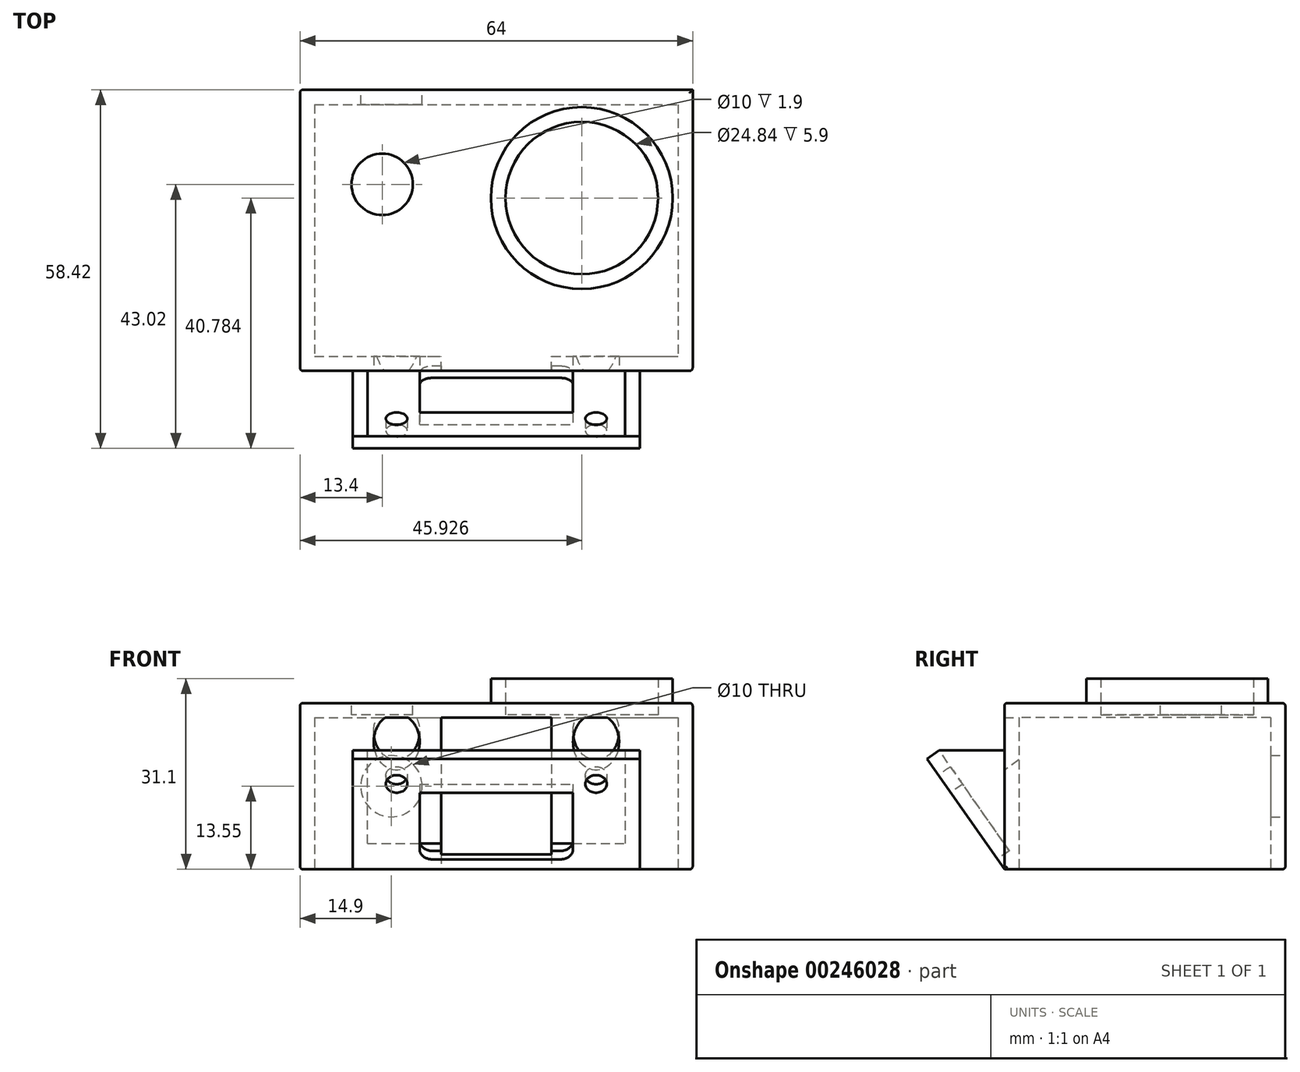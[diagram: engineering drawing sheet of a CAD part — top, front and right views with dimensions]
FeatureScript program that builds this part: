
annotation { "Feature Type Name" : "Feature", "Feature Type Description" : "" }
export const myFeature = defineFeature(function(context is Context, id is Id, definition is map)
    precondition{}
    {
        {
            assignVariable(context, id + "F0", {"name" : "goproThickness", "anyValue" : 24.7});
        }
        {
            assignVariable(context, id + "F1", {"name" : "lensDepth", "anyValue" : 4});
        }
        {
            assignVariable(context, id + "F2", {"name" : "caseThickness", "anyValue" : 2.4});
        }
        {
            assignVariable(context, id + "F3", {"name" : "webThickness", "anyValue" : 0.5});
        }
        {
            assignVariable(context, id + "F4", {"name" : "cameraTilt", "anyValue" : 35});
        }
        {
            var Q0;
            Q0=qCreatedBy(makeId("Top.planeOp"),FACE);
            var sketch = newSketch(context, id + "F5", { "sketchPlane" : qUnion([Q0])});
            skLineSegment(sketch, "E0.bottom", {"start": v(-29.6, 20.5) * mm, "end": v(29.6, 20.5) * mm});
            skLineSegment(sketch, "E0.top", {"start": v(-29.6, -20.5) * mm, "end": v(29.6, -20.5) * mm});
            skLineSegment(sketch, "E0.left", {"start": v(-29.6, 20.5) * mm, "end": v(-29.6, -20.5) * mm});
            skLineSegment(sketch, "E0.right", {"start": v(29.6, 20.5) * mm, "end": v(29.6, -20.5) * mm});
            skPoint(sketch, "E0.middle", {"position": v(0, 0) * mm});
            skLineSegment(sketch, "E1.0", {"start": v(-32, 22.9) * mm, "end": v(32, 22.9) * mm});
            skLineSegment(sketch, "E1.1", {"start": v(-32, 22.9) * mm, "end": v(-32, -22.9) * mm});
            skLineSegment(sketch, "E1.2", {"start": v(-32, -22.9) * mm, "end": v(32, -22.9) * mm});
            skLineSegment(sketch, "E1.3", {"start": v(32, 22.9) * mm, "end": v(32, -22.9) * mm});
            skSolve(sketch);
        }
        {
            var Q0;
            Q0 = qSketchRegion(id + "F5", true);
            extrude(context, id + "F6", {"entities" : qUnion([Q0]), "depth" : (getVariable(context, 'goproThickness')) * mm});
        }
        {
            var Q0;
            Q0=makeQuery(id+"F6.opExtrude","CAP_FACE",FACE,{"disambiguationData":[OSD([sQuery(id+"F5.wireOp",EDGE,"E0.bottom"),sQuery(id+"F5.wireOp",EDGE,"E0.top"),sQuery(id+"F5.wireOp",EDGE,"E0.left"),sQuery(id+"F5.wireOp",EDGE,"E0.right"),sQuery(id+"F5.wireOp",EDGE,"E1.0"),sQuery(id+"F5.wireOp",EDGE,"E1.1"),sQuery(id+"F5.wireOp",EDGE,"E1.2"),sQuery(id+"F5.wireOp",EDGE,"E1.3")])],"isStart":false});
            var sketch = newSketch(context, id + "F7", { "sketchPlane" : qUnion([Q0])});
            skLineSegment(sketch, "E2.bottom", {"start": v(-29.6, 20.5) * mm, "end": v(29.6, 20.5) * mm});
            skLineSegment(sketch, "E2.top", {"start": v(-29.6, -20.5) * mm, "end": v(29.6, -20.5) * mm});
            skLineSegment(sketch, "E2.left", {"start": v(-29.6, 20.5) * mm, "end": v(-29.6, -20.5) * mm});
            skLineSegment(sketch, "E2.right", {"start": v(29.6, 20.5) * mm, "end": v(29.6, -20.5) * mm});
            skPoint(sketch, "E2.middle", {"position": v(0, 0) * mm});
            skLineSegment(sketch, "E3.bottom", {"start": v(-32, 22.9) * mm, "end": v(32, 22.9) * mm});
            skLineSegment(sketch, "E3.top", {"start": v(-32, -22.9) * mm, "end": v(32, -22.9) * mm});
            skLineSegment(sketch, "E3.left", {"start": v(-32, 22.9) * mm, "end": v(-32, -22.9) * mm});
            skLineSegment(sketch, "E3.right", {"start": v(32, 22.9) * mm, "end": v(32, -22.9) * mm});
            skSolve(sketch);
        }
        {
            var Q0;
            Q0 = qSketchRegion(id + "F7", true);
            var Q1;
            Q1=makeQuery(id+"F7.imprint","IMPRINT",FACE,{"disambiguationData":[TD([[makeQuery(id+"F7.imprint","IMPRINT",EDGE,{"derivedFrom":sQuery(id+"F7.wireOp",EDGE,"E2.bottom")}),-1.0]])]});
            extrude(context, id + "F8", {"entities" : qUnion([Q0, Q1]), "operationType" : NewBodyOperationType.ADD, "depth" : (getVariable(context, 'caseThickness')) * mm});
        }
        {
            var Q0;
            Q0=makeQuery(id+"F8.opExtrude","CAP_FACE",FACE,{"disambiguationData":[OSD([sQuery(id+"F7.wireOp",EDGE,"E3.bottom"),sQuery(id+"F7.wireOp",EDGE,"E3.top"),sQuery(id+"F7.wireOp",EDGE,"E3.left"),sQuery(id+"F7.wireOp",EDGE,"E3.right")])],"isStart":false});
            var sketch = newSketch(context, id + "F9", { "sketchPlane" : qUnion([Q0])});
            skCircle(sketch, "E4", {"center": v(-18.6, 7.5) * mm, "radius": 5 * mm});
            skSolve(sketch);
        }
        {
            var Q0;
            Q0 = qSketchRegion(id + "F9", true);
            extrude(context, id + "F10", {"entities" : qUnion([Q0]), "operationType" : NewBodyOperationType.REMOVE, "oppositeDirection" : true, "depth" : (getVariable(context, 'caseThickness') - getVariable(context, 'webThickness')) * mm});
        }
        {
            var Q0;
            Q0=makeQuery(id+"F8.opExtrude","CAP_FACE",FACE,{"disambiguationData":[OSD([sQuery(id+"F7.wireOp",EDGE,"E3.bottom"),sQuery(id+"F7.wireOp",EDGE,"E3.top"),sQuery(id+"F7.wireOp",EDGE,"E3.left"),sQuery(id+"F7.wireOp",EDGE,"E3.right")])],"isStart":false});
            var sketch = newSketch(context, id + "F11", { "sketchPlane" : qUnion([Q0])});
            skCircle(sketch, "E5", {"center": v(13.93, 5.26) * mm, "radius": 12.42 * mm});
            skCircle(sketch, "E6", {"center": v(13.93, 5.26) * mm, "radius": 14.82 * mm});
            skSolve(sketch);
        }
        {
            var Q0;
            Q0 = qSketchRegion(id + "F11", true);
            extrude(context, id + "F12", {"entities" : qUnion([Q0]), "operationType" : NewBodyOperationType.ADD, "depth" : (getVariable(context, 'lensDepth')) * mm});
        }
        {
            var Q0;
            Q0=makeQuery(id+"F12.boolean.opBoolean","SPLIT",FACE,{"disambiguationData":[TD([makeQuery(id+"F12.opExtrude","SWEPT_FACE",FACE,{"disambiguationData":[OSD([sQuery(id+"F11.wireOp",EDGE,"E5")])]})])],"derivedFrom":makeQuery(id+"F8.opExtrude","CAP_FACE",FACE,{"disambiguationData":[OSD([sQuery(id+"F7.wireOp",EDGE,"E3.bottom"),sQuery(id+"F7.wireOp",EDGE,"E3.top"),sQuery(id+"F7.wireOp",EDGE,"E3.left"),sQuery(id+"F7.wireOp",EDGE,"E3.right")])],"isStart":false})});
            extrude(context, id + "F13", {"entities" : qUnion([Q0]), "operationType" : NewBodyOperationType.REMOVE, "oppositeDirection" : true, "depth" : (getVariable(context, 'caseThickness') - getVariable(context, 'webThickness')) * mm});
        }
        {
            var Q0;
            Q0=makeQuery(id+"F8.boolean.opBoolean","MERGE",FACE,{"derivedFrom":[makeQuery(id+"F6.opExtrude","SWEPT_FACE",FACE,{"disambiguationData":[OSD([sQuery(id+"F5.wireOp",EDGE,"E1.0")])]}),makeQuery(id+"F8.opExtrude","SWEPT_FACE",FACE,{"disambiguationData":[OSD([sQuery(id+"F7.wireOp",EDGE,"E3.bottom")])]})]});
            var sketch = newSketch(context, id + "F14", { "sketchPlane" : qUnion([Q0])});
            skCircle(sketch, "E7", {"center": v(17.1, 13.55) * mm, "radius": 5 * mm});
            skPoint(sketch, "E7.centerSnap0", {"position": v(32, 13.55) * mm});
            skSolve(sketch);
        }
        {
            var Q0;
            Q0 = qSketchRegion(id + "F14", true);
            extrude(context, id + "F15", {"entities" : qUnion([Q0]), "operationType" : NewBodyOperationType.REMOVE, "oppositeDirection" : true, "depth" : (getVariable(context, 'caseThickness')) * mm});
        }
        {
            var Q0;
            Q0=makeQuery(id+"F6.opExtrude","CAP_EDGE",EDGE,{"disambiguationData":[OSD([sQuery(id+"F5.wireOp",EDGE,"E1.2")])],"isStart":true});
            cPlane(context, id + "F16", {"entities" : qUnion([Q0]), "cplaneType" : CPlaneType.LINE_ANGLE, "offset" : 25 * mm, "angle" : (getVariable(context, 'cameraTilt')) * degree, "width" : 150 * mm, "height" : 150 * mm});
        }
        {
            var Q0;
            Q0=qCreatedBy(id+"F16.planeOp",FACE);
            var sketch = newSketch(context, id + "F17", { "sketchPlane" : qUnion([Q0])});
            skLineSegment(sketch, "E8", {"start": v(0, 13.13) * mm, "end": v(21, 13.13) * mm});
            skLineSegment(sketch, "E9", {"start": v(21, 13.13) * mm, "end": v(21, 35.13) * mm});
            skLineSegment(sketch, "E10", {"start": v(21, 35.13) * mm, "end": v(-21, 35.13) * mm});
            skLineSegment(sketch, "E11", {"start": v(-21, 35.13) * mm, "end": v(-21, 13.13) * mm});
            skLineSegment(sketch, "E12", {"start": v(-21, 13.13) * mm, "end": v(0, 13.13) * mm});
            skLineSegment(sketch, "E13", {"start": v(0, 35.13) * mm, "end": v(0, 24.13) * mm});
            skPoint(sketch, "E13.endSnap0", {"position": v(21, 24.13) * mm});
            skLineSegment(sketch, "E14", {"start": v(0, 24.13) * mm, "end": v(0, 13.13) * mm});
            skCircle(sketch, "E15", {"center": v(16.25, 30.13) * mm, "radius": 1.75 * mm});
            skCircle(sketch, "E16.MirrorC", {"center": v(-16.25, 30.13) * mm, "radius": 1.75 * mm});
            skSolve(sketch);
        }
        {
            var Q0;
            Q0=makeQuery(id+"F17.imprint","IMPRINT",FACE,{"disambiguationData":[TD([[makeQuery(id+"F17.imprint","IMPRINT",EDGE,{"derivedFrom":sQuery(id+"F17.wireOp",EDGE,"E8")}),1.0]])]});
            var Q1;
            {var subQ0=sQuery(id+"F17.wireOp",EDGE,"E11");Q1=makeQuery(id+"F17.imprint","IMPRINT",FACE,{"disambiguationData":[TD([[makeQuery(id+"F17.imprint","IMPRINT",EDGE,{"derivedFrom":subQ0}),1.0]])]});}
            extrude(context, id + "F18", {"entities" : qUnion([Q0, Q1]), "operationType" : NewBodyOperationType.ADD, "depth" : (getVariable(context, 'caseThickness')) * mm});
        }
        {
            var Q0;
            Q0=makeQuery(id+"F18.opExtrude","SWEPT_FACE",FACE,{"disambiguationData":[OSD([sQuery(id+"F17.wireOp",EDGE,"E9")])]});
            var sketch = newSketch(context, id + "F19", { "sketchPlane" : qUnion([Q0])});
            skLineSegment(sketch, "E17", {"start": v(35.52, 18.02) * mm, "end": v(33.55, 19.4) * mm});
            skLineSegment(sketch, "E18", {"start": v(22.9, 0) * mm, "end": v(35.52, 18.02) * mm});
            skLineSegment(sketch, "E19", {"start": v(33.55, 19.4) * mm, "end": v(22.9, 19.4) * mm});
            skLineSegment(sketch, "E20", {"start": v(22.9, 19.4) * mm, "end": v(22.9, 0) * mm});
            skSolve(sketch);
        }
        {
            var Q0;
            Q0 = qSketchRegion(id + "F19", true);
            extrude(context, id + "F20", {"entities" : qUnion([Q0]), "operationType" : NewBodyOperationType.ADD, "depth" : (getVariable(context, 'caseThickness')) * mm});
        }
        {
            var Q0;
            Q0=makeQuery(id+"F18.opExtrude","SWEPT_FACE",FACE,{"disambiguationData":[OSD([sQuery(id+"F17.wireOp",EDGE,"E11")])]});
            var sketch = newSketch(context, id + "F21", { "sketchPlane" : qUnion([Q0])});
            skLineSegment(sketch, "E21", {"start": v(-22.9, 0) * mm, "end": v(-35.52, 18.02) * mm});
            skLineSegment(sketch, "E22", {"start": v(-35.52, 18.02) * mm, "end": v(-33.55, 19.4) * mm});
            skLineSegment(sketch, "E23", {"start": v(-33.55, 19.4) * mm, "end": v(-22.9, 19.4) * mm});
            skLineSegment(sketch, "E24", {"start": v(-22.9, 19.4) * mm, "end": v(-22.9, 0) * mm});
            skSolve(sketch);
        }
        {
            var Q0;
            Q0 = qSketchRegion(id + "F21", true);
            extrude(context, id + "F22", {"entities" : qUnion([Q0]), "operationType" : NewBodyOperationType.ADD, "depth" : (getVariable(context, 'caseThickness')) * mm});
        }
        {
            var Q0;
            Q0=makeQuery(id+"F22.boolean.opBoolean","MERGE",FACE,{"derivedFrom":[makeQuery(id+"F20.boolean.opBoolean","MERGE",FACE,{"derivedFrom":[makeQuery(id+"F18.opExtrude","CAP_FACE",FACE,{"disambiguationData":[OSD([sQuery(id+"F17.wireOp",EDGE,"E8"),sQuery(id+"F17.wireOp",EDGE,"E9"),sQuery(id+"F17.wireOp",EDGE,"E10"),sQuery(id+"F17.wireOp",EDGE,"E11"),sQuery(id+"F17.wireOp",EDGE,"E12"),sQuery(id+"F17.wireOp",EDGE,"E15"),sQuery(id+"F17.wireOp",EDGE,"E16.MirrorC")])],"isStart":true}),makeQuery(id+"F20.opExtrude","SWEPT_FACE",FACE,{"disambiguationData":[OSD([sQuery(id+"F19.wireOp",EDGE,"E18")])]})]}),makeQuery(id+"F22.opExtrude","SWEPT_FACE",FACE,{"disambiguationData":[OSD([sQuery(id+"F21.wireOp",EDGE,"E21")])]})]});
            var sketch = newSketch(context, id + "F23", { "sketchPlane" : qUnion([Q0])});
            skCircle(sketch, "E25", {"center": v(-16.25, 30.13) * mm, "radius": 1.75 * mm});
            skCircle(sketch, "E26.MirrorC", {"center": v(16.25, 30.13) * mm, "radius": 1.75 * mm});
            skSolve(sketch);
        }
        {
            var Q0;
            Q0 = qSketchRegion(id + "F23", true);
            var Q1;
            Q1=makeQuery(id+"F8.opExtrude","CAP_FACE",FACE,{"disambiguationData":[OSD([sQuery(id+"F7.wireOp",EDGE,"E3.bottom"),sQuery(id+"F7.wireOp",EDGE,"E3.top"),sQuery(id+"F7.wireOp",EDGE,"E3.left"),sQuery(id+"F7.wireOp",EDGE,"E3.right")])],"isStart":true});
            extrude(context, id + "F24", {"entities" : qUnion([Q0]), "operationType" : NewBodyOperationType.REMOVE, "endBound" : BoundingType.UP_TO_SURFACE, "oppositeDirection" : true, "endBoundEntityFace" : qUnion([Q1]), "depth" : 25 * mm});
        }
        {
            var Q0;
            Q0=makeQuery(id+"F8.opExtrude","CAP_EDGE",EDGE,{"disambiguationData":[OSD([sQuery(id+"F7.wireOp",EDGE,"E3.left")])],"isStart":false});
            var Q1;
            Q1=makeQuery(id+"F8.opExtrude","CAP_EDGE",EDGE,{"disambiguationData":[OSD([sQuery(id+"F7.wireOp",EDGE,"E3.top")])],"isStart":false});
            var Q2;
            Q2=makeQuery(id+"F8.opExtrude","CAP_EDGE",EDGE,{"disambiguationData":[OSD([sQuery(id+"F7.wireOp",EDGE,"E3.right")])],"isStart":false});
            var Q3;
            Q3=makeQuery(id+"F8.opExtrude","CAP_EDGE",EDGE,{"disambiguationData":[OSD([sQuery(id+"F7.wireOp",EDGE,"E3.bottom")])],"isStart":false});
            var Q4;
            Q4=makeQuery(id+"F10.boolean.opBoolean","COPY",EDGE,{"derivedFrom":makeQuery(id+"F10.opExtrude","CAP_EDGE",EDGE,{"disambiguationData":[OSD([sQuery(id+"F9.wireOp",EDGE,"E4")])],"isStart":true})});
            var Q5;
            Q5=makeQuery(id+"F6.opExtrude","CAP_EDGE",EDGE,{"disambiguationData":[OSD([sQuery(id+"F5.wireOp",EDGE,"E1.3")])],"isStart":true});
            var Q6;
            Q6=makeQuery(id+"F6.opExtrude","CAP_EDGE",EDGE,{"disambiguationData":[OSD([sQuery(id+"F5.wireOp",EDGE,"E1.0")])],"isStart":true});
            var Q7;
            Q7=makeQuery(id+"F8.boolean.opBoolean","MERGE",EDGE,{"derivedFrom":[makeQuery(id+"F6.opExtrude","SWEPT_EDGE",EDGE,{"disambiguationData":[OSD([sQuery(id+"F5.wireOp",EDGE,"E1.0"),sQuery(id+"F5.wireOp",EDGE,"E1.1")])]}),makeQuery(id+"F8.opExtrude","SWEPT_EDGE",EDGE,{"disambiguationData":[OSD([sQuery(id+"F7.wireOp",EDGE,"E3.bottom"),sQuery(id+"F7.wireOp",EDGE,"E3.left")])]})]});
            var Q8;
            Q8=makeQuery(id+"F6.opExtrude","CAP_EDGE",EDGE,{"disambiguationData":[OSD([sQuery(id+"F5.wireOp",EDGE,"E1.1")])],"isStart":true});
            var Q9;
            Q9=makeQuery(id+"F8.boolean.opBoolean","MERGE",EDGE,{"derivedFrom":[makeQuery(id+"F6.opExtrude","SWEPT_EDGE",EDGE,{"disambiguationData":[OSD([sQuery(id+"F5.wireOp",EDGE,"E1.1"),sQuery(id+"F5.wireOp",EDGE,"E1.2")])]}),makeQuery(id+"F8.opExtrude","SWEPT_EDGE",EDGE,{"disambiguationData":[OSD([sQuery(id+"F7.wireOp",EDGE,"E3.top"),sQuery(id+"F7.wireOp",EDGE,"E3.left")])]})]});
            var Q10;
            Q10=makeQuery(id+"F8.boolean.opBoolean","MERGE",EDGE,{"derivedFrom":[makeQuery(id+"F6.opExtrude","SWEPT_EDGE",EDGE,{"disambiguationData":[OSD([sQuery(id+"F5.wireOp",EDGE,"E1.2"),sQuery(id+"F5.wireOp",EDGE,"E1.3")])]}),makeQuery(id+"F8.opExtrude","SWEPT_EDGE",EDGE,{"disambiguationData":[OSD([sQuery(id+"F7.wireOp",EDGE,"E3.top"),sQuery(id+"F7.wireOp",EDGE,"E3.right")])]})]});
            fillet(context, id + "F25", {"entities" : qUnion([Q0, Q1, Q2, Q3, Q4, Q5, Q6, Q7, Q8, Q9, Q10]), "radius" : 0.5 * mm, "tangentPropagation" : true, "allowEdgeOverflow" : false});
        }
        {
            var Q0;
            Q0=makeQuery(id+"F6.opExtrude","CAP_FACE",FACE,{"disambiguationData":[OSD([sQuery(id+"F5.wireOp",EDGE,"E0.bottom"),sQuery(id+"F5.wireOp",EDGE,"E0.top"),sQuery(id+"F5.wireOp",EDGE,"E0.left"),sQuery(id+"F5.wireOp",EDGE,"E0.right"),sQuery(id+"F5.wireOp",EDGE,"E1.0"),sQuery(id+"F5.wireOp",EDGE,"E1.1"),sQuery(id+"F5.wireOp",EDGE,"E1.2"),sQuery(id+"F5.wireOp",EDGE,"E1.3")])],"isStart":true});
            var sketch = newSketch(context, id + "F26", { "sketchPlane" : qUnion([Q0])});
            skLineSegment(sketch, "E27.bottom", {"start": v(-9, 22.9) * mm, "end": v(9, 22.9) * mm});
            skLineSegment(sketch, "E27.top", {"start": v(-9, 20.5) * mm, "end": v(9, 20.5) * mm});
            skLineSegment(sketch, "E27.left", {"start": v(-9, 22.9) * mm, "end": v(-9, 20.5) * mm});
            skLineSegment(sketch, "E27.right", {"start": v(9, 22.9) * mm, "end": v(9, 20.5) * mm});
            skPoint(sketch, "E27.middle", {"position": v(0, 21.7) * mm});
            skSolve(sketch);
        }
        {
            var Q0;
            Q0 = qSketchRegion(id + "F26", true);
            var Q1;
            Q1=makeQuery(id+"F8.opExtrude","CAP_FACE",FACE,{"disambiguationData":[OSD([sQuery(id+"F7.wireOp",EDGE,"E3.bottom"),sQuery(id+"F7.wireOp",EDGE,"E3.top"),sQuery(id+"F7.wireOp",EDGE,"E3.left"),sQuery(id+"F7.wireOp",EDGE,"E3.right")])],"isStart":true});
            extrude(context, id + "F27", {"entities" : qUnion([Q0]), "operationType" : NewBodyOperationType.REMOVE, "endBound" : BoundingType.UP_TO_SURFACE, "oppositeDirection" : true, "endBoundEntityFace" : qUnion([Q1]), "depth" : 25 * mm});
        }
        {
            var Q0;
            Q0=makeQuery(id+"F18.opExtrude","CAP_FACE",FACE,{"disambiguationData":[OSD([sQuery(id+"F17.wireOp",EDGE,"E8"),sQuery(id+"F17.wireOp",EDGE,"E9"),sQuery(id+"F17.wireOp",EDGE,"E10"),sQuery(id+"F17.wireOp",EDGE,"E11"),sQuery(id+"F17.wireOp",EDGE,"E12"),sQuery(id+"F17.wireOp",EDGE,"E15"),sQuery(id+"F17.wireOp",EDGE,"E16.MirrorC")])],"isStart":false});
            var sketch = newSketch(context, id + "F28", { "sketchPlane" : qUnion([Q0])});
            skCircle(sketch, "E28", {"center": v(16.25, 30.13) * mm, "radius": 3.75 * mm});
            skCircle(sketch, "E29.MirrorC", {"center": v(-16.25, 30.13) * mm, "radius": 3.75 * mm});
            skSolve(sketch);
        }
        {
            var Q0;
            Q0 = qSketchRegion(id + "F28", true);
            var Q1;
            {var subQ0=sQuery(id+"F7.wireOp",EDGE,"E3.right");var subQ1=sQuery(id+"F7.wireOp",EDGE,"E3.left");var subQ2=sQuery(id+"F7.wireOp",EDGE,"E3.top");var subQ3=sQuery(id+"F7.wireOp",EDGE,"E3.bottom");Q1=makeQuery(id+"F27.boolean.opBoolean","MERGE",FACE,{"derivedFrom":[makeQuery(id+"F8.opExtrude","CAP_FACE",FACE,{"disambiguationData":[OSD([subQ3,subQ2,subQ1,subQ0])],"isStart":true}),makeQuery(id+"F27.opExtrude","CAP_FACE",FACE,{"disambiguationData":[OSD([subQ3,subQ2,subQ1,subQ0])],"isStart":false})]});}
            extrude(context, id + "F29", {"entities" : qUnion([Q0]), "operationType" : NewBodyOperationType.REMOVE, "endBound" : BoundingType.UP_TO_SURFACE, "endBoundEntityFace" : qUnion([Q1]), "depth" : 25 * mm});
        }
        {
            var Q0;
            Q0=makeQuery(id+"F22.boolean.opBoolean","MERGE",FACE,{"derivedFrom":[makeQuery(id+"F20.boolean.opBoolean","MERGE",FACE,{"derivedFrom":[makeQuery(id+"F18.opExtrude","CAP_FACE",FACE,{"disambiguationData":[OSD([sQuery(id+"F17.wireOp",EDGE,"E8"),sQuery(id+"F17.wireOp",EDGE,"E9"),sQuery(id+"F17.wireOp",EDGE,"E10"),sQuery(id+"F17.wireOp",EDGE,"E11"),sQuery(id+"F17.wireOp",EDGE,"E12"),sQuery(id+"F17.wireOp",EDGE,"E15"),sQuery(id+"F17.wireOp",EDGE,"E16.MirrorC")])],"isStart":true}),makeQuery(id+"F20.opExtrude","SWEPT_FACE",FACE,{"disambiguationData":[OSD([sQuery(id+"F19.wireOp",EDGE,"E18")])]})]}),makeQuery(id+"F22.opExtrude","SWEPT_FACE",FACE,{"disambiguationData":[OSD([sQuery(id+"F21.wireOp",EDGE,"E21")])]})]});
            var sketch = newSketch(context, id + "F30", { "sketchPlane" : qUnion([Q0])});
            skPoint(sketch, "E30", {"position": v(-16.25, 30.13) * mm});
            skPoint(sketch, "E31", {"position": v(16.25, 30.13) * mm});
            skLineSegment(sketch, "E32", {"start": v(-12.5, 28.38) * mm, "end": v(-12.5, 15.13) * mm});
            skLineSegment(sketch, "E33", {"start": v(-12.5, 15.13) * mm, "end": v(0, 15.13) * mm});
            skLineSegment(sketch, "E34", {"start": v(0, 15.13) * mm, "end": v(12.5, 15.13) * mm});
            skLineSegment(sketch, "E35", {"start": v(12.5, 15.13) * mm, "end": v(12.5, 28.38) * mm});
            skLineSegment(sketch, "E36", {"start": v(-12.5, 28.38) * mm, "end": v(12.5, 28.38) * mm});
            skLineSegment(sketch, "E37", {"start": v(-12.5, 28.38) * mm, "end": v(-20.09, 28.38) * mm});
            skSolve(sketch);
        }
        {
            var Q0;
            Q0 = qSketchRegion(id + "F30", true);
            var Q1;
            {var subQ1=sQuery(id+"F30.wireOp",EDGE,"BaOD2BEO-CHPW-Bun6-DBrZ-VnkcG4sa4ueP");Q1=makeQuery(id+"F30.imprint","IMPRINT",FACE,{"disambiguationData":[TD([[makeQuery(id+"F30.imprint","IMPRINT",EDGE,{"derivedFrom":subQ1}),1.0]])]});}
            extrude(context, id + "F31", {"entities" : qUnion([Q0, Q1]), "operationType" : NewBodyOperationType.REMOVE, "oppositeDirection" : true, "depth" : (getVariable(context, 'caseThickness')) * mm});
        }
        {
            var Q0;
            Q0=makeQuery(id+"F31.boolean.opBoolean","COPY",EDGE,{"derivedFrom":makeQuery(id+"F31.opExtrude","SWEPT_EDGE",EDGE,{"disambiguationData":[OSD([sQuery(id+"F30.wireOp",EDGE,"E32"),sQuery(id+"F30.wireOp",EDGE,"E33")])]})});
            var Q1;
            Q1=makeQuery(id+"F31.boolean.opBoolean","COPY",EDGE,{"derivedFrom":makeQuery(id+"F31.opExtrude","SWEPT_EDGE",EDGE,{"disambiguationData":[OSD([sQuery(id+"F30.wireOp",EDGE,"E34"),sQuery(id+"F30.wireOp",EDGE,"E35")])]})});
            fillet(context, id + "F32", {"entities" : qUnion([Q0, Q1]), "radius" : 2 * mm, "tangentPropagation" : true, "allowEdgeOverflow" : false});
        }
        {
            var Q0;
            Q0=makeQuery(id+"F12.opExtrude","CAP_FACE",FACE,{"disambiguationData":[OSD([sQuery(id+"F11.wireOp",EDGE,"E5"),sQuery(id+"F11.wireOp",EDGE,"E6")])],"isStart":false});
            cPlane(context, id + "F33", {"entities" : qUnion([Q0]), "cplaneType" : CPlaneType.OFFSET, "offset" : 0 * mm, "width" : 150 * mm, "height" : 150 * mm});
        }
    });
